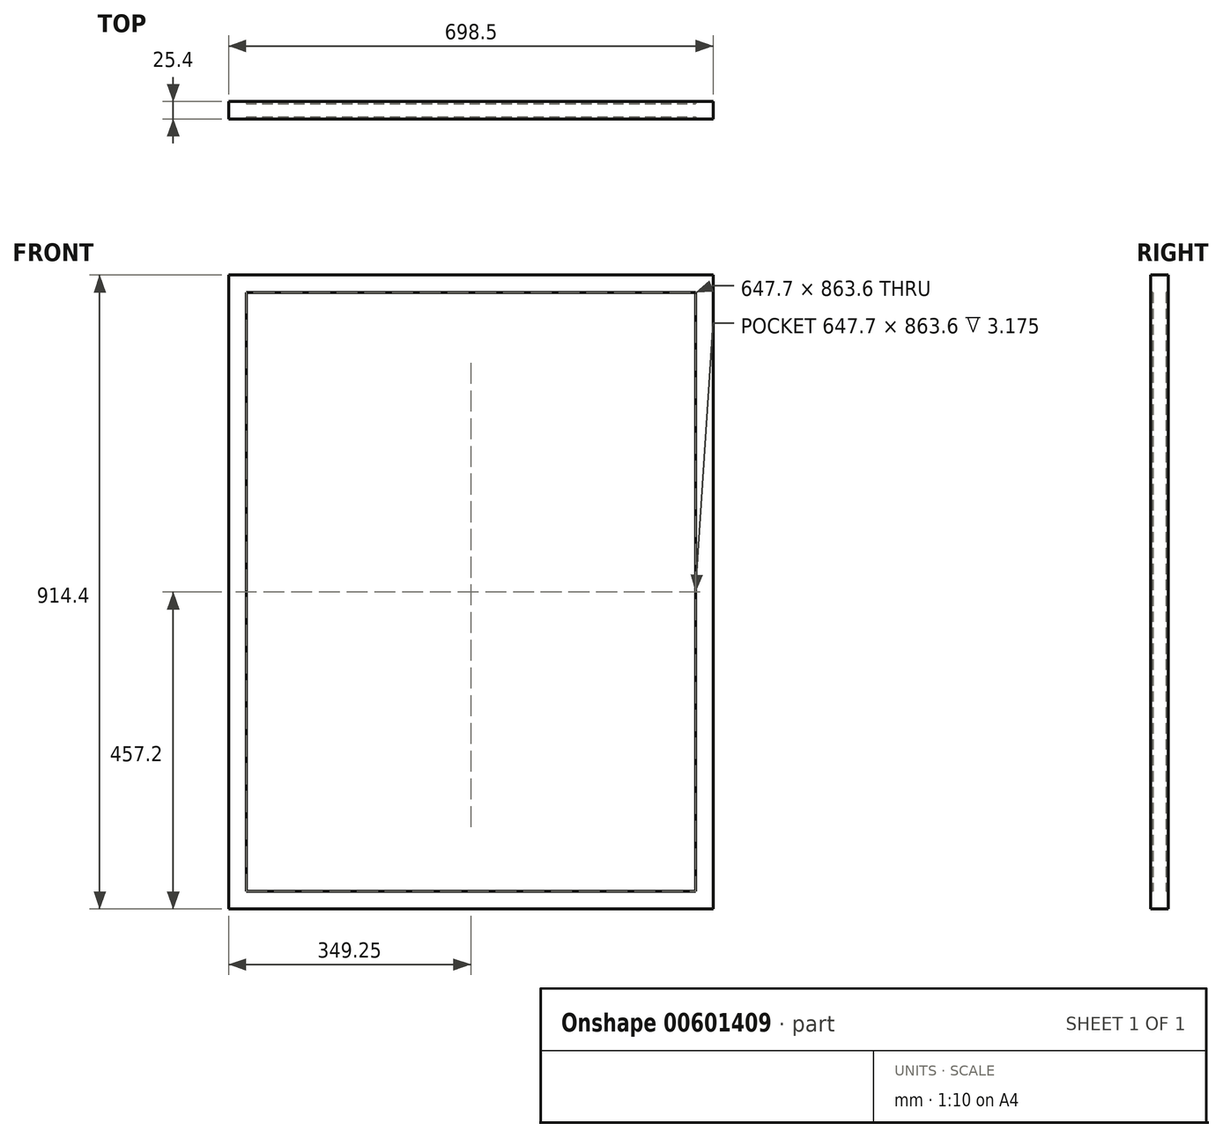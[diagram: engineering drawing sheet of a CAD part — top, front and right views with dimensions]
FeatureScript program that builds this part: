
annotation { "Feature Type Name" : "Feature", "Feature Type Description" : "" }
export const myFeature = defineFeature(function(context is Context, id is Id, definition is map)
    precondition{}
    {
        {
            var Q0;
            Q0=qCreatedBy(makeId("Front.planeOp"),FACE);
            var sketch = newSketch(context, id + "F0", { "sketchPlane" : qUnion([Q0])});
            skLineSegment(sketch, "E0.bottom", {"start": v(0, 0) * mm, "end": v(-698.5, 0) * mm});
            skLineSegment(sketch, "E0.top", {"start": v(0, 914.4) * mm, "end": v(-698.5, 914.4) * mm});
            skLineSegment(sketch, "E0.left", {"start": v(0, 0) * mm, "end": v(0, 914.4) * mm});
            skLineSegment(sketch, "E0.right", {"start": v(-698.5, 0) * mm, "end": v(-698.5, 914.4) * mm});
            skLineSegment(sketch, "E1.bottom", {"start": v(-673.1, 889) * mm, "end": v(-25.4, 889) * mm});
            skLineSegment(sketch, "E1.top", {"start": v(-673.1, 25.4) * mm, "end": v(-25.4, 25.4) * mm});
            skLineSegment(sketch, "E1.left", {"start": v(-673.1, 889) * mm, "end": v(-673.1, 25.4) * mm});
            skLineSegment(sketch, "E1.right", {"start": v(-25.4, 889) * mm, "end": v(-25.4, 25.4) * mm});
            skSolve(sketch);
        }
        {
            var Q0;
            Q0=makeQuery(id+"F0.imprint","IMPRINT",FACE,{"disambiguationData":[TD([[makeQuery(id+"F0.imprint","IMPRINT",EDGE,{"derivedFrom":sQuery(id+"F0.wireOp",EDGE,"E0.bottom")}),-1.0]])]});
            extrude(context, id + "F1", {"entities" : qUnion([Q0]), "endBound" : BoundingType.SYMMETRIC, "oppositeDirection" : true, "depth" : 25.4 * mm, "offsetDistance" : 25.4 * mm});
        }
        {
            var Q0;
            Q0=makeQuery(id+"F0.imprint","IMPRINT",FACE,{"disambiguationData":[TD([[makeQuery(id+"F0.imprint","IMPRINT",EDGE,{"derivedFrom":sQuery(id+"F0.wireOp",EDGE,"E1.bottom")}),-1.0]])]});
            extrude(context, id + "F2", {"entities" : qUnion([Q0]), "operationType" : NewBodyOperationType.ADD, "endBound" : BoundingType.SYMMETRIC, "depth" : 19.05 * mm, "offsetDistance" : 25.4 * mm});
        }
    });
